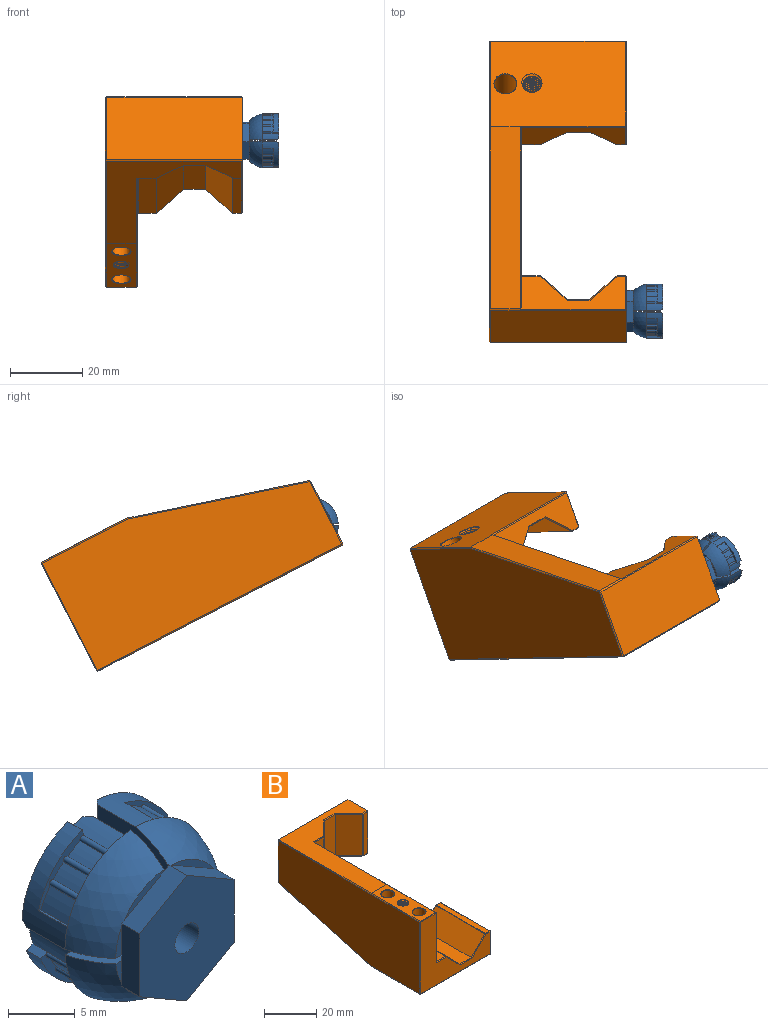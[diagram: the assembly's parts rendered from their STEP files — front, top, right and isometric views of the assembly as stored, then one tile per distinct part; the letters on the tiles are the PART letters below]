
ASSEMBLY  parts=2 mates=1
PART A: 104 faces, bbox 15.1x12.9x15.1 mm
  f0: cylinder r=1.27mm len=2.54mm, axis (0,-1,0), area 16.1mm2, adj f7,f8,f9,f10,f11,f12,f13,f14
  f1: plane 5x2.89mm, normal (0.5,0,0.87), area 11mm2, adj f2,f6,f7,f93,f101,f103
  f2: plane 5x2.89mm, normal (-0.5,0,0.87), area 11mm2, adj f1,f3,f7,f94,f95,f103
  f3: plane 5.77x1.91mm, normal (-1,0,0), area 11mm2, adj f2,f4,f8,f91,f94,f99,f100,f103
  f4: plane 5x2.89mm, normal (-0.5,0,-0.87), area 11mm2, adj f3,f5,f9,f91,f102,f103
  f5: plane 5x2.89mm, normal (0.5,0,-0.87), area 11mm2, adj f4,f6,f9,f92,f98,f103
  f6: plane 5.77x1.91mm, normal (1,0,0), area 11mm2, adj f1,f5,f24,f92,f93,f96,f97,f103
  f7: plane 4.61x0.74mm, normal (0,1,0), area 2.2mm2, adj f0,f1,f2,f15,f21,f26
  f8: plane 3.84x0.51mm, normal (0,1,0), area 1.9mm2, adj f0,f3,f17,f18
  f9: plane 4.61x0.74mm, normal (0,1,0), area 2.2mm2, adj f0,f4,f5,f16,f19,f25
  f10: sphere r=5.21mm, area 55.1mm2, adj f0,f16,f18,f30
  f11: sphere r=5.21mm, area 55.1mm2, adj f0,f14,f19,f31
  f12: sphere r=5.21mm, area 55.1mm2, adj f0,f15,f20,f32
  f13: sphere r=5.21mm, area 55.1mm2, adj f0,f17,f21,f42
  f14: plane 7.61x6.23mm, normal (0,0,1), area 21mm2, adj f0,f11,f23,f24,f31,f40,f84,f97
  f15: plane 7.61x6.23mm, normal (-1,0,0), area 21mm2, adj f0,f7,f12,f26,f32,f54,f87
  f16: plane 7.61x6.23mm, normal (1,0,0), area 21mm2, adj f0,f9,f10,f25,f30,f78,f86
  f17: plane 7.61x6.23mm, normal (0,0,-1), area 21mm2, adj f0,f8,f13,f22,f42,f66,f90,f100
  f18: plane 7.61x6.32mm, normal (0,0,1), area 18mm2, adj f0,f8,f10,f25,f30,f75,f76,f89
  f19: plane 7.61x6.32mm, normal (-1,0,0), area 18mm2, adj f0,f9,f11,f23,f31,f37,f38,f85
  f20: plane 7.61x6.32mm, normal (0,0,-1), area 18mm2, adj f0,f12,f24,f26,f32,f51,f52,f83
  f21: plane 7.61x6.32mm, normal (1,0,0), area 18mm2, adj f0,f7,f13,f22,f42,f63,f64,f88
  f22: sphere r=7.68mm, area 40.7mm2, adj f17,f21,f63,f66,f94,f95,f100
  f23: sphere r=7.68mm, area 40.7mm2, adj f14,f19,f37,f40,f92,f97,f98
  f24: plane 3.84x0.51mm, normal (0,1,0), area 1.9mm2, adj f0,f6,f14,f20
  f25: sphere r=7.68mm, area 40.7mm2, adj f9,f16,f18,f75,f78,f91,f99,f102
  f26: sphere r=7.68mm, area 40.7mm2, adj f7,f15,f20,f51,f54,f93,f96,f101
  f27: plane 6.52x6.47mm, normal (0,1,0), area 11.8mm2, adj f30,f76,f78,f79,f86,f89
  f28: plane 6.52x6.47mm, normal (0,1,0), area 11.8mm2, adj f31,f38,f40,f43,f84,f85
  f29: plane 6.52x6.47mm, normal (0,1,0), area 11.8mm2, adj f32,f52,f54,f55,f83,f87
  f30: cone r=4.71mm half-angle=64.5deg, axis (0,1,0), area 11.6mm2, adj f10,f16,f18,f27,f86,f89
  f31: cone r=4.71mm half-angle=64.5deg, axis (0,1,0), area 11.6mm2, adj f11,f14,f19,f28,f84,f85
  f32: cone r=4.71mm half-angle=64.5deg, axis (0,1,0), area 11.6mm2, adj f12,f15,f20,f29,f83,f87
  f33: cylinder r=8.14mm len=3.05mm, axis (0,1,0), area 4.7mm2, adj f37,f39,f45,f46
  f34: cylinder r=8.14mm len=3.05mm, axis (0,1,0), area 6.1mm2, adj f36,f37,f39,f46
  f35: cylinder r=8.14mm len=3.05mm, axis (0,1,0), area 4.7mm2, adj f37,f39,f44,f45
  f36: plane 3.05x0.25mm, normal (-0.26,0,-0.97), area 0.8mm2, adj f34,f37,f39,f40
  f37: plane 6.74x5.63mm, normal (0,1,0), area 5.3mm2, adj f19,f23,f33,f34,f35,f36,f38,f44
  f38: cylinder r=6.74mm len=4.57mm, axis (0,1,0), area 8.7mm2, adj f19,f28,f37,f43,f44,f85
  f39: plane 5.17x4.87mm, normal (0,-1,0), area 3.7mm2, adj f33,f34,f35,f36,f40,f43,f44,f45
  f40: cylinder r=7.5mm len=7.03mm, axis (0,1,0), area 19.7mm2, adj f14,f23,f28,f36,f39,f43,f84
  f41: plane 6.52x6.47mm, normal (0,1,0), area 11.8mm2, adj f42,f64,f66,f67,f88,f90
  f42: cone r=4.71mm half-angle=64.5deg, axis (0,1,0), area 11.6mm2, adj f13,f17,f21,f41,f88,f90
  f43: plane 1.52x0.72mm, normal (-0.95,0,-0.32), area 1.2mm2, adj f28,f38,f39,f40
  f44: cylinder r=0.25mm len=3.05mm, axis (0,1,0), area 2.5mm2, adj f35,f37,f38,f39
  f45: cylinder r=0.25mm len=3.05mm, axis (0,1,0), area 2.5mm2, adj f33,f35,f37,f39
  f46: cylinder r=0.25mm len=3.05mm, axis (0,1,0), area 2.5mm2, adj f33,f34,f37,f39
  f47: cylinder r=8.14mm len=3.05mm, axis (0,1,0), area 4.7mm2, adj f51,f53,f57,f58
  f48: cylinder r=8.14mm len=3.05mm, axis (0,1,0), area 6.1mm2, adj f50,f51,f53,f58
  f49: cylinder r=8.14mm len=3.05mm, axis (0,1,0), area 4.7mm2, adj f51,f53,f56,f57
  f50: plane 3.05x0.25mm, normal (0.97,0,-0.26), area 0.8mm2, adj f48,f51,f53,f54
  f51: plane 6.74x5.63mm, normal (0,1,0), area 5.3mm2, adj f20,f26,f47,f48,f49,f50,f52,f56
  f52: cylinder r=6.74mm len=4.57mm, axis (0,1,0), area 8.7mm2, adj f20,f29,f51,f55,f56,f83
  f53: plane 5.17x4.87mm, normal (0,-1,0), area 3.7mm2, adj f47,f48,f49,f50,f54,f55,f56,f57
  f54: cylinder r=7.5mm len=7.03mm, axis (0,1,0), area 19.7mm2, adj f15,f26,f29,f50,f53,f55,f87
  f55: plane 1.52x0.72mm, normal (0.32,0,-0.95), area 1.2mm2, adj f29,f52,f53,f54
  f56: cylinder r=0.25mm len=3.05mm, axis (0,1,0), area 2.5mm2, adj f49,f51,f52,f53
  f57: cylinder r=0.25mm len=3.05mm, axis (0,1,0), area 2.5mm2, adj f47,f49,f51,f53
  f58: cylinder r=0.25mm len=3.05mm, axis (0,1,0), area 2.5mm2, adj f47,f48,f51,f53
  f59: cylinder r=8.14mm len=3.05mm, axis (0,1,0), area 4.7mm2, adj f63,f65,f69,f70
  f60: cylinder r=8.14mm len=3.05mm, axis (0,1,0), area 6.1mm2, adj f62,f63,f65,f70
  f61: cylinder r=8.14mm len=3.05mm, axis (0,1,0), area 4.7mm2, adj f63,f65,f68,f69
  f62: plane 3.05x0.25mm, normal (0.26,0,0.97), area 0.8mm2, adj f60,f63,f65,f66
  f63: plane 6.74x5.63mm, normal (0,1,0), area 5.3mm2, adj f21,f22,f59,f60,f61,f62,f64,f68
  f64: cylinder r=6.74mm len=4.57mm, axis (0,1,0), area 8.7mm2, adj f21,f41,f63,f67,f68,f88
  f65: plane 5.17x4.87mm, normal (0,-1,0), area 3.7mm2, adj f59,f60,f61,f62,f66,f67,f68,f69
  f66: cylinder r=7.5mm len=7.03mm, axis (0,1,0), area 19.7mm2, adj f17,f22,f41,f62,f65,f67,f90
  f67: plane 1.52x0.72mm, normal (0.95,0,0.32), area 1.2mm2, adj f41,f64,f65,f66
  f68: cylinder r=0.25mm len=3.05mm, axis (0,1,0), area 2.5mm2, adj f61,f63,f64,f65
  f69: cylinder r=0.25mm len=3.05mm, axis (0,1,0), area 2.5mm2, adj f59,f61,f63,f65
  f70: cylinder r=0.25mm len=3.05mm, axis (0,1,0), area 2.5mm2, adj f59,f60,f63,f65
  f71: cylinder r=8.14mm len=3.05mm, axis (0,1,0), area 4.7mm2, adj f75,f77,f81,f82
  f72: cylinder r=8.14mm len=3.05mm, axis (0,1,0), area 6.1mm2, adj f74,f75,f77,f82
  f73: cylinder r=8.14mm len=3.05mm, axis (0,1,0), area 4.7mm2, adj f75,f77,f80,f81
  f74: plane 3.05x0.25mm, normal (-0.97,0,0.26), area 0.8mm2, adj f72,f75,f77,f78
  f75: plane 6.74x5.63mm, normal (0,1,0), area 5.3mm2, adj f18,f25,f71,f72,f73,f74,f76,f80
  f76: cylinder r=6.74mm len=4.57mm, axis (0,1,0), area 8.7mm2, adj f18,f27,f75,f79,f80,f89
  f77: plane 5.17x4.87mm, normal (0,-1,0), area 3.7mm2, adj f71,f72,f73,f74,f78,f79,f80,f81
  f78: cylinder r=7.5mm len=7.03mm, axis (0,1,0), area 19.7mm2, adj f16,f25,f27,f74,f77,f79,f86
  f79: plane 1.52x0.72mm, normal (-0.32,0,0.95), area 1.2mm2, adj f27,f76,f77,f78
  f80: cylinder r=0.25mm len=3.05mm, axis (0,1,0), area 2.5mm2, adj f73,f75,f76,f77
  f81: cylinder r=0.25mm len=3.05mm, axis (0,1,0), area 2.5mm2, adj f71,f73,f75,f77
  f82: cylinder r=0.25mm len=3.05mm, axis (0,1,0), area 2.5mm2, adj f71,f72,f75,f77
  f83: plane 1.76x0.54mm, normal (0,0.71,-0.71), area 0.9mm2, adj f20,f29,f32,f52
  f84: plane 2.54x0.57mm, normal (0,0.71,0.71), area 1.4mm2, adj f14,f28,f31,f40
  f85: plane 1.76x0.54mm, normal (-0.71,0.71,0), area 0.9mm2, adj f19,f28,f31,f38
  f86: plane 2.54x0.57mm, normal (0.71,0.71,0), area 1.4mm2, adj f16,f27,f30,f78
  f87: plane 2.54x0.57mm, normal (-0.71,0.71,0), area 1.4mm2, adj f15,f29,f32,f54
  f88: plane 1.76x0.54mm, normal (0.71,0.71,0), area 0.9mm2, adj f21,f41,f42,f64
  f89: plane 1.76x0.54mm, normal (0,0.71,0.71), area 0.9mm2, adj f18,f27,f30,f76
  f90: plane 2.54x0.57mm, normal (0,0.71,-0.71), area 1.4mm2, adj f17,f41,f42,f66
  f91: plane 0.41x0.24mm, normal (0,1,0), area 0mm2, adj f3,f4,f25
  f92: plane 0.41x0.24mm, normal (0,1,0), area 0mm2, adj f5,f6,f23
  f93: plane 0.41x0.24mm, normal (0,1,0), area 0mm2, adj f1,f6,f26
  f94: plane 0.41x0.24mm, normal (0,1,0), area 0mm2, adj f2,f3,f22
  f95: plane 4.26x2.6mm, normal (0,-1,0), area 2.3mm2, adj f2,f21,f22
  f96: plane 2.11x0.62mm, normal (0,-1,0), area 0.8mm2, adj f6,f20,f26
  f97: plane 2.62x0.64mm, normal (0,-1,0), area 1.1mm2, adj f6,f14,f23
  f98: plane 4.26x2.6mm, normal (0,-1,0), area 2.3mm2, adj f5,f19,f23
  f99: plane 2.11x0.62mm, normal (0,-1,0), area 0.8mm2, adj f3,f18,f25
  f100: plane 2.62x0.64mm, normal (0,-1,0), area 1.1mm2, adj f3,f17,f22
  f101: plane 4.54x2.62mm, normal (0,-1,0), area 2.3mm2, adj f1,f26
  f102: plane 4.54x2.62mm, normal (0,-1,0), area 2.3mm2, adj f4,f25
  f103: plane 11.55x10mm, normal (0,-1,0), area 81.5mm2, adj f0,f1,f2,f3,f4,f5,f6
PART B: 108 faces, bbox 38.3x77.1x35.1 mm
  f0: plane 49.15x33.42mm, normal (1,0,0), area 1111.3mm2, adj f1,f2,f4,f25,f68,f74,f76,f79
  f1: plane 5.36x0.36mm, normal (0,0.71,0.71), area 1.9mm2, adj f0,f2,f4,f24,f45,f54,f55
  f2: plane 0.29x0.11mm, normal (0.71,0.71,0), area 0mm2, adj f0,f1,f54
  f3: plane 29.25x0.29mm, normal (0,0.71,-0.71), area 10.4mm2, adj f4,f5,f50,f57,f107
  f4: plane 28.86x10.41mm, normal (0,1,0), area 197.1mm2, adj f0,f1,f3,f45,f47,f48,f49,f50
  f5: plane 37.55x26.82mm, normal (0,0,-1), area 932.2mm2, adj f3,f14,f42,f51,f57,f62,f64,f65
  f6: cylinder r=2.6mm len=5.21mm, axis (0,0,-1), area 10mm2, adj f13,f33,f63,f64,f65
  f7: cylinder r=2.6mm len=5.21mm, axis (0,0,-1), area 5.1mm2, adj f8,f14,f64,f65
  f8: cylinder r=2.6mm len=5.21mm, axis (0,0,-1), area 7.4mm2, adj f7,f9,f64,f65
  f9: cylinder r=2.6mm len=5.21mm, axis (0,0,-1), area 7.4mm2, adj f8,f10,f64,f65
  f10: cylinder r=2.6mm len=5.21mm, axis (0,0,-1), area 7.4mm2, adj f9,f11,f64,f65
  f11: cylinder r=2.6mm len=5.21mm, axis (0,0,-1), area 7.4mm2, adj f10,f12,f64,f65
  f12: cylinder r=2.6mm len=5.21mm, axis (0,0,-1), area 7.4mm2, adj f11,f13,f64,f65
  f13: cylinder r=2.6mm len=5.21mm, axis (0,0,-1), area 7.4mm2, adj f6,f12,f64,f65
  f14: cone r=2.6mm half-angle=45deg, axis (0,0,-1), area 1.2mm2, adj f5,f7,f64,f65
  f15: plane 26.54x8.41mm, normal (0,0,1), area 159.5mm2, adj f17,f43,f52,f53,f59,f60,f61,f66
  f16: plane 6.32x6.32mm, normal (0,0,-1), area 15.1mm2, adj f18,f32,f59,f60,f61
  f17: cone r=1.91mm half-angle=45deg, axis (0,0,1), area 0.9mm2, adj f15,f18,f60,f61
  f18: cylinder r=1.91mm len=8.76mm, axis (0,0,1), area 34.8mm2, adj f16,f17,f60,f61
  f19: plane 26.42x10.41mm, normal (1,0,0), area 275.1mm2, adj f40,f50,f57,f58
  f20: plane 26.42x2.33mm, normal (0,0,1), area 61.6mm2, adj f38,f49,f56,f58
  f21: plane 26.42x7.39mm, normal (-0.71,0,0.71), area 276.2mm2, adj f22,f36,f48,f56
  f22: plane 26.42x6.1mm, normal (0,0,1), area 161mm2, adj f21,f23,f34,f47
  f23: plane 26.42x7.39mm, normal (0.71,0,0.71), area 276.2mm2, adj f22,f35,f45,f55
  f24: plane 26.42x4.97mm, normal (0,0,1), area 131.4mm2, adj f1,f37,f54,f55
  f25: plane 26.42x22.56mm, normal (1,0,0), area 595.8mm2, adj f0,f39,f54,f77
  f26: plane 76.37x33.44mm, normal (-1,0,0), area 2205.9mm2, adj f44,f99,f101,f103,f104,f105
  f27: plane 37.44x33.53mm, normal (0,-1,0), area 480.8mm2, adj f34,f35,f36,f37,f38,f39,f40,f42
  f28: cylinder r=2.54mm len=27.97mm, axis (0,0,1), area 446.3mm2, adj f29,f53
  f29: plane 5.08x5.08mm, normal (0,0,1), area 20.3mm2, adj f28
  f30: cylinder r=2.54mm len=27.97mm, axis (0,0,1), area 446.3mm2, adj f31,f52
  f31: plane 5.08x5.08mm, normal (0,0,1), area 20.3mm2, adj f30
  f32: cylinder r=3.05mm len=25.02mm, axis (0,0,-1), area 479.1mm2, adj f16,f51
  f33: plane 5.21x5.21mm, normal (0,0,-1), area 21.3mm2, adj f6
  f34: plane 6.31x0.25mm, normal (0,-0.71,0.71), area 2.2mm2, adj f22,f27,f35,f36
  f35: plane 7.71x7.58mm, normal (0.5,-0.71,0.5), area 3.8mm2, adj f23,f27,f34,f37,f55
  f36: plane 7.71x7.58mm, normal (-0.5,-0.71,0.5), area 3.8mm2, adj f21,f27,f34,f38,f56
  f37: plane 5.62x0.36mm, normal (0,-0.71,0.71), area 2mm2, adj f24,f27,f35,f39,f54,f55
  f38: plane 2.65x0.29mm, normal (0,-0.71,0.71), area 0.9mm2, adj f20,f27,f36,f40,f56,f58
  f39: plane 23.15x0.36mm, normal (0.71,-0.71,0), area 8.3mm2, adj f25,f27,f37,f41,f54,f77
  f40: plane 10.81x0.29mm, normal (0.71,-0.71,0), area 3.8mm2, adj f19,f27,f38,f42,f57,f58
  f41: plane 0.2x0.2mm, normal (0.58,-0.58,0.58), area 0mm2, adj f39,f43,f77
  f42: plane 37.76x0.29mm, normal (0,-0.71,-0.71), area 13.5mm2, adj f5,f27,f40,f44,f57,f104
  f43: plane 8.38x0.25mm, normal (0,-0.71,0.71), area 3mm2, adj f15,f27,f41,f46,f77,f99
  f44: plane 33.63x0.25mm, normal (-0.71,-0.71,0), area 12.1mm2, adj f26,f27,f42,f46,f99,f104
  f45: plane 7.71x7.58mm, normal (0.5,0.71,0.5), area 3.8mm2, adj f1,f4,f23,f47,f55
  f46: plane 0.21x0.21mm, normal (-0.58,-0.58,0.58), area 0mm2, adj f43,f44,f99
  f47: plane 6.31x0.25mm, normal (0,0.71,0.71), area 2.2mm2, adj f4,f22,f45,f48
  f48: plane 7.71x7.58mm, normal (-0.5,0.71,0.5), area 3.8mm2, adj f4,f21,f47,f49,f56
  f49: plane 2.65x0.29mm, normal (0,0.71,0.71), area 0.9mm2, adj f4,f20,f48,f50,f56,f58
  f50: plane 10.81x0.29mm, normal (0.71,0.71,0), area 3.8mm2, adj f3,f4,f19,f49,f57,f58
  f51: cone r=3.05mm half-angle=45deg, axis (0,0,-1), area 3.5mm2, adj f5,f32
  f52: cone r=2.54mm half-angle=45deg, axis (0,0,1), area 2.9mm2, adj f15,f30
  f53: cone r=2.54mm half-angle=45deg, axis (0,0,1), area 2.9mm2, adj f15,f28
  f54: cylinder r=0.25mm len=26.42mm, axis (0,-1,0), area 10.5mm2, adj f1,f2,f24,f25,f37,f39
  f55: cylinder r=0.25mm len=26.45mm, axis (0,1,0), area 5.3mm2, adj f1,f23,f24,f35,f37,f45
  f56: cylinder r=0.25mm len=26.45mm, axis (0,1,0), area 5.3mm2, adj f20,f21,f36,f38,f48,f49
  f57: cylinder r=0.25mm len=26.56mm, axis (0,1,0), area 10.6mm2, adj f3,f5,f19,f40,f42,f50
  f58: cylinder r=0.25mm len=26.56mm, axis (0,1,0), area 10.6mm2, adj f19,f20,f38,f40,f49,f50
  f59: cylinder r=2.41mm len=8.89mm, axis (0,0,1), area 16.9mm2, adj f15,f16,f60,f61
  f60: bspline ~9.74x4.93mm, area 66.9mm2, adj f15,f16,f17,f18,f59
  f61: bspline ~9.61x4.93mm, area 66.9mm2, adj f15,f16,f17,f18,f59
  f62: cylinder r=3.17mm len=8.7mm, axis (0,0,-1), area 21.8mm2, adj f5,f63,f64,f65
  f63: cone r=2.22mm half-angle=45deg, axis (0,0,-1), area 5.5mm2, adj f6,f62,f64,f65
  f64: bspline ~11.06x6.46mm, area 55.6mm2, adj f5,f6,f7,f8,f9,f10,f11,f12
  f65: bspline ~9.76x6.46mm, area 84.9mm2, adj f5,f6,f7,f8,f9,f10,f11,f12
  f66: plane 49.97x37.46mm, normal (0,0,1), area 611.6mm2, adj f15,f79,f82,f86,f88,f92,f96,f98
  f67: plane 37.74x19.4mm, normal (0,1,0), area 732.2mm2, adj f73,f100,f103,f106
  f68: plane 19.4x5.2mm, normal (0,-1,0), area 100.9mm2, adj f0,f76,f81,f82
  f69: plane 19.4x7.39mm, normal (0.71,-0.71,0), area 202.8mm2, adj f70,f80,f81,f86
  f70: plane 19.4x6.11mm, normal (0,-1,0), area 118.5mm2, adj f69,f71,f83,f88
  f71: plane 19.4x7.41mm, normal (-0.7,-0.71,0), area 202.6mm2, adj f70,f85,f91,f92
  f72: plane 19.4x2.32mm, normal (0,-1,0), area 45.1mm2, adj f90,f91,f95,f96
  f73: plane 19.4x10.62mm, normal (1,0,0), area 206mm2, adj f67,f89,f95,f98
  f74: plane 29.08x10.33mm, normal (0,0,-1), area 194.6mm2, adj f0,f76,f80,f83,f85,f89,f90,f106
  f75: plane 49.58x13.91mm, normal (0,0.27,-0.96), area 426.8mm2, adj f5,f105,f106,f107
  f76: plane 5.2x0.32mm, normal (0,-0.71,-0.71), area 2.2mm2, adj f0,f68,f74,f78
  f77: plane 26.47x0.31mm, normal (0.71,0,0.71), area 11.5mm2, adj f15,f25,f39,f41,f43,f79
  f78: plane 0.3x0.3mm, normal (0.28,-0.68,-0.68), area 0mm2, adj f76,f80,f81
  f79: plane 39.65x0.3mm, normal (0.71,0,0.71), area 16.8mm2, adj f0,f66,f77,f82
  f80: plane 7.69x7.61mm, normal (0.5,-0.5,-0.71), area 4.5mm2, adj f69,f74,f78,f83
  f81: plane 19.4x0.21mm, normal (0.38,-0.92,0), area 4.5mm2, adj f68,f69,f78,f84
  f82: plane 5.5x0.32mm, normal (0,-0.71,0.71), area 2.3mm2, adj f66,f68,f79,f84
  f83: plane 6.35x0.33mm, normal (0,-0.71,-0.71), area 2.6mm2, adj f70,f74,f80,f85
  f84: plane 0.3x0.3mm, normal (0.28,-0.68,0.68), area 0mm2, adj f81,f82,f86
  f85: plane 7.66x7.62mm, normal (-0.5,-0.5,-0.71), area 4.5mm2, adj f71,f74,f83,f87
  f86: plane 7.69x7.61mm, normal (0.5,-0.5,0.71), area 4.5mm2, adj f66,f69,f84,f88
  f87: plane 0.3x0.3mm, normal (-0.28,-0.68,-0.68), area 0mm2, adj f85,f90,f91
  f88: plane 6.35x0.33mm, normal (0,-0.71,0.71), area 2.6mm2, adj f66,f70,f86,f92
  f89: plane 10.62x0.3mm, normal (0.71,0,-0.71), area 4.4mm2, adj f73,f74,f93,f106
  f90: plane 2.32x0.3mm, normal (0,-0.71,-0.71), area 1mm2, adj f72,f74,f87,f93
  f91: plane 19.4x0.21mm, normal (-0.38,-0.92,0), area 4.4mm2, adj f71,f72,f87,f94
  f92: plane 7.66x7.62mm, normal (-0.5,-0.5,0.71), area 4.5mm2, adj f66,f71,f88,f94
  f93: plane 0.3x0.3mm, normal (0.58,-0.58,-0.58), area 0.1mm2, adj f89,f90,f95
  f94: plane 0.3x0.3mm, normal (-0.28,-0.68,0.68), area 0mm2, adj f91,f92,f96
  f95: plane 19.4x0.3mm, normal (0.71,-0.71,0), area 8.2mm2, adj f72,f73,f93,f97
  f96: plane 2.32x0.3mm, normal (0,-0.71,0.71), area 1mm2, adj f66,f72,f94,f97
  f97: plane 0.3x0.3mm, normal (0.58,-0.58,0.58), area 0.1mm2, adj f95,f96,f98
  f98: plane 10.62x0.3mm, normal (0.71,0,0.71), area 4.4mm2, adj f66,f73,f97,f100
  f99: plane 26.47x0.31mm, normal (-0.71,0,0.71), area 11.2mm2, adj f15,f26,f43,f44,f46,f101
  f100: plane 37.74x0.3mm, normal (0,0.71,0.71), area 15.9mm2, adj f66,f67,f98,f102
  f101: plane 49.96x0.31mm, normal (-0.71,0,0.71), area 21.2mm2, adj f26,f66,f99,f102
  f102: plane 0.3x0.3mm, normal (-0.58,0.58,0.58), area 0.1mm2, adj f100,f101,f103
  f103: plane 19.57x0.3mm, normal (-0.71,0.71,0), area 8.3mm2, adj f26,f67,f102,f105,f106
  f104: plane 26.82x0.3mm, normal (-0.71,0,-0.71), area 11.3mm2, adj f5,f26,f42,f44,f105
  f105: plane 49.87x14.26mm, normal (-0.71,0.19,-0.68), area 21.9mm2, adj f26,f75,f103,f104,f106
  f106: plane 37.92x0.42mm, normal (0,0.71,-0.71), area 17.4mm2, adj f67,f74,f75,f89,f103,f105,f107
  f107: plane 49.95x14.03mm, normal (0.71,0.19,-0.68), area 21.8mm2, adj f0,f3,f4,f5,f74,f75,f106
PLACE A rot(axis=(0.58,0.58,-0.56),121.1deg) t=(35.62,45.55,18.04)mm
PLACE B rot(axis=(1,0,0),152.7deg) t=(8.57,96.68,19.9)mm
MATE parallel A.f0 <-> B.f73  axis (-1,0,0) through (46.62,45.55,18.04)mm
